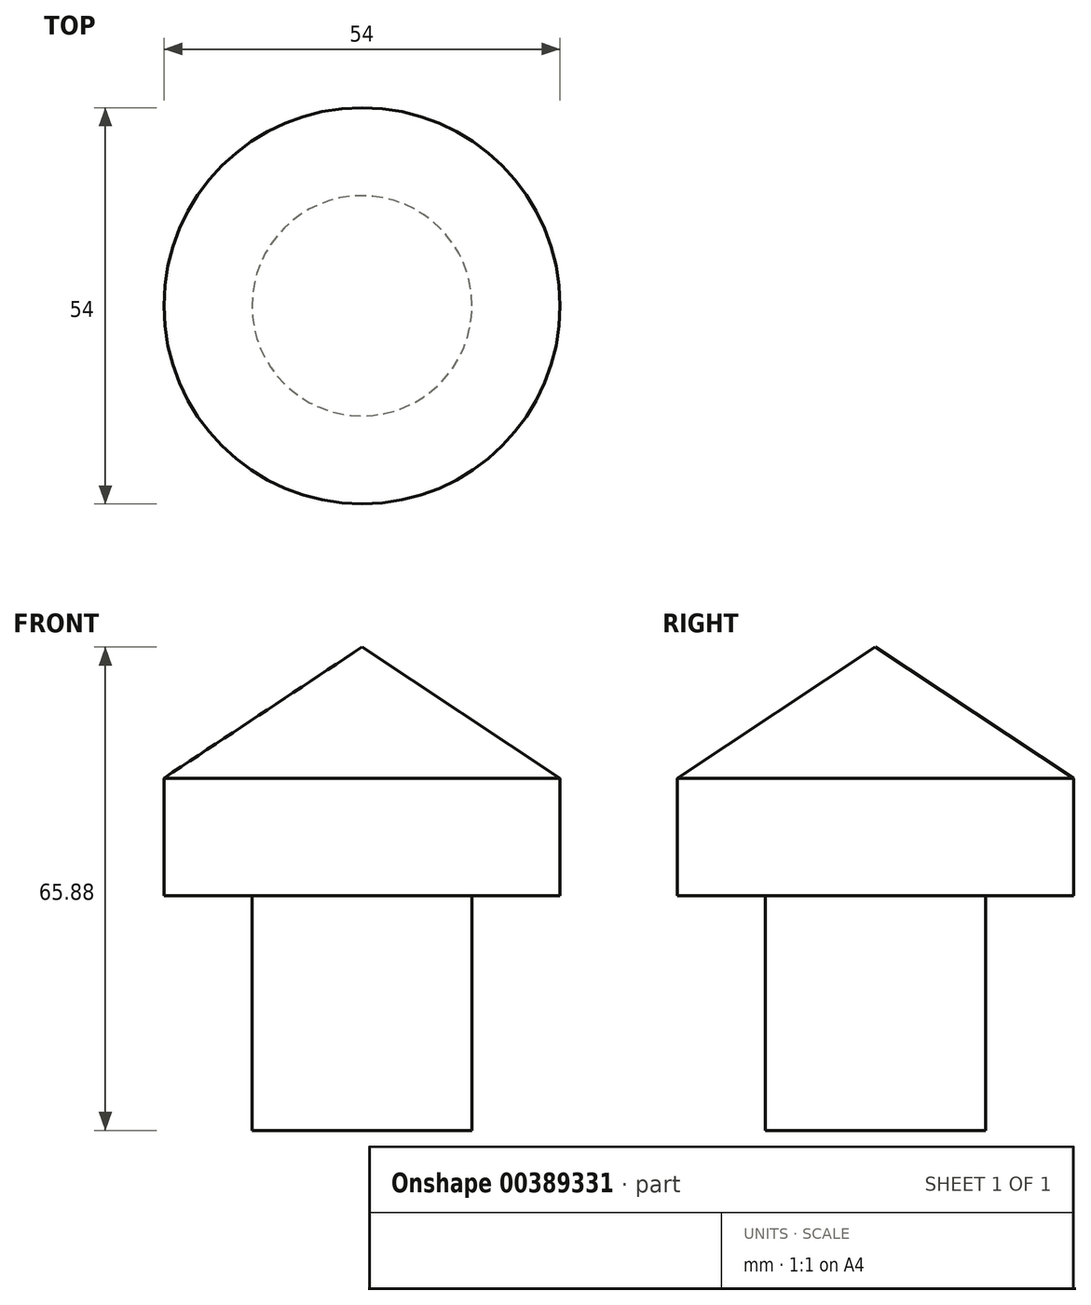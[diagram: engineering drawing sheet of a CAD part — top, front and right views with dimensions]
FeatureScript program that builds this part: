
annotation { "Feature Type Name" : "Feature", "Feature Type Description" : "" }
export const myFeature = defineFeature(function(context is Context, id is Id, definition is map)
    precondition{}
    {
        {
            var Q0;
            Q0=qCreatedBy(makeId("Front.planeOp"),FACE);
            var sketch = newSketch(context, id + "F0", { "sketchPlane" : qUnion([Q0])});
            skLineSegment(sketch, "E0", {"start": v(0, -32) * mm, "end": v(-15, -32) * mm});
            skLineSegment(sketch, "E1", {"start": v(-15, -32) * mm, "end": v(-15, 0) * mm});
            skLineSegment(sketch, "E2", {"start": v(-15, 0) * mm, "end": v(-27, 0) * mm});
            skLineSegment(sketch, "E3", {"start": v(-27, 0) * mm, "end": v(-27, 16) * mm});
            skLineSegment(sketch, "E4", {"start": v(-27, 16) * mm, "end": v(0, 33.88) * mm});
            skLineSegment(sketch, "E5", {"start": v(0, 33.88) * mm, "end": v(0, -32) * mm});
            skSolve(sketch);
        }
        {
            var Q0;
            Q0 = qSketchRegion(id + "F0", true);
            var Q1;
            Q1=sQuery(id+"F0.wireOp",EDGE,"E5");
            revolve(context, id + "F1", {"entities" : qUnion([Q0]), "axis" : qUnion([Q1]), "revolveType" : RevolveType.FULL});
        }
    });
